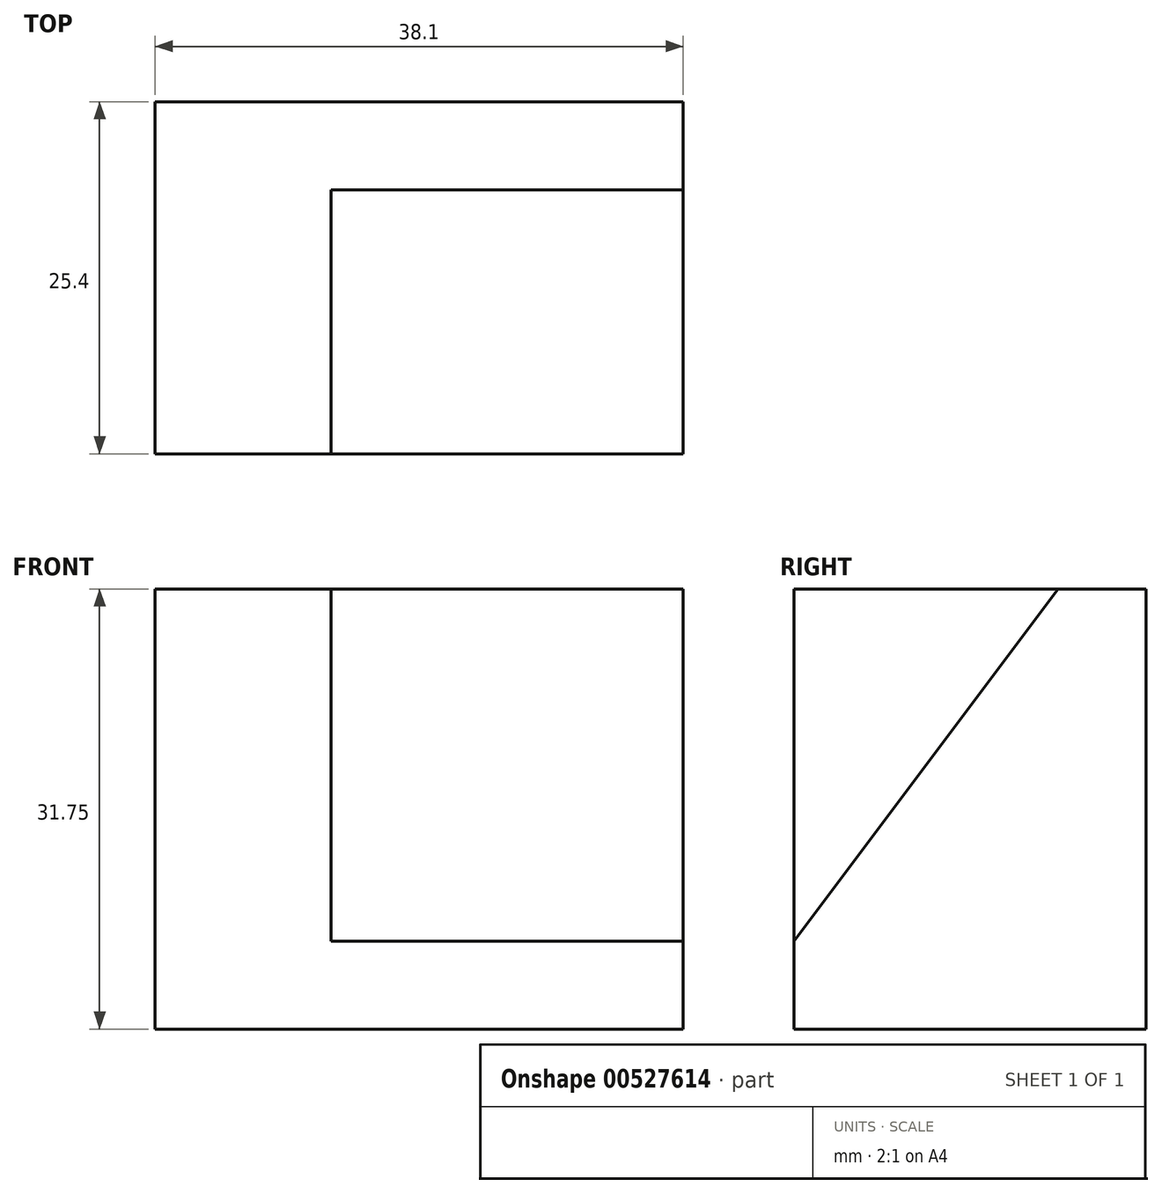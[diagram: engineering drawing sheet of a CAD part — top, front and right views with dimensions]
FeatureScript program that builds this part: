
annotation { "Feature Type Name" : "Feature", "Feature Type Description" : "" }
export const myFeature = defineFeature(function(context is Context, id is Id, definition is map)
    precondition{}
    {
        {
            var Q0;
            Q0=qCreatedBy(makeId("Front.planeOp"),FACE);
            var sketch = newSketch(context, id + "F0", { "sketchPlane" : qUnion([Q0])});
            skLineSegment(sketch, "E0.bottom", {"start": v(-21.46, 35.87) * mm, "end": v(16.64, 35.87) * mm});
            skLineSegment(sketch, "E0.top", {"start": v(-21.46, 4.12) * mm, "end": v(16.64, 4.12) * mm});
            skLineSegment(sketch, "E0.left", {"start": v(-21.46, 35.87) * mm, "end": v(-21.46, 4.12) * mm});
            skLineSegment(sketch, "E0.right", {"start": v(16.64, 35.87) * mm, "end": v(16.64, 4.12) * mm});
            skSolve(sketch);
        }
        {
            var Q0;
            Q0=makeQuery(id+"F0.imprint","IMPRINT",FACE,{"disambiguationData":[TD([[makeQuery(id+"F0.imprint","IMPRINT",EDGE,{"derivedFrom":sQuery(id+"F0.wireOp",EDGE,"E0.bottom")}),-1.0]])]});
            extrude(context, id + "F1", {"entities" : qUnion([Q0]), "depth" : 25.4 * mm, "offsetDistance" : 25.4 * mm});
        }
        {
            var Q0;
            Q0=makeQuery(id+"F1.opExtrude","SWEPT_FACE",FACE,{"disambiguationData":[OSD([sQuery(id+"F0.wireOp",EDGE,"E0.right")])]});
            var sketch = newSketch(context, id + "F2", { "sketchPlane" : qUnion([Q0])});
            skLineSegment(sketch, "E1", {"start": v(-6.35, 35.87) * mm, "end": v(-25.4, 10.47) * mm});
            skLineSegment(sketch, "E2", {"start": v(-25.4, 10.47) * mm, "end": v(-25.4, 35.87) * mm});
            skLineSegment(sketch, "E3", {"start": v(-25.4, 35.87) * mm, "end": v(-6.35, 35.87) * mm});
            skSolve(sketch);
        }
        {
            var Q0;
            Q0 = qSketchRegion(id + "F2", true);
            extrude(context, id + "F3", {"entities" : qUnion([Q0]), "operationType" : NewBodyOperationType.REMOVE, "oppositeDirection" : true, "depth" : 25.4 * mm, "offsetDistance" : 25.4 * mm});
        }
    });
